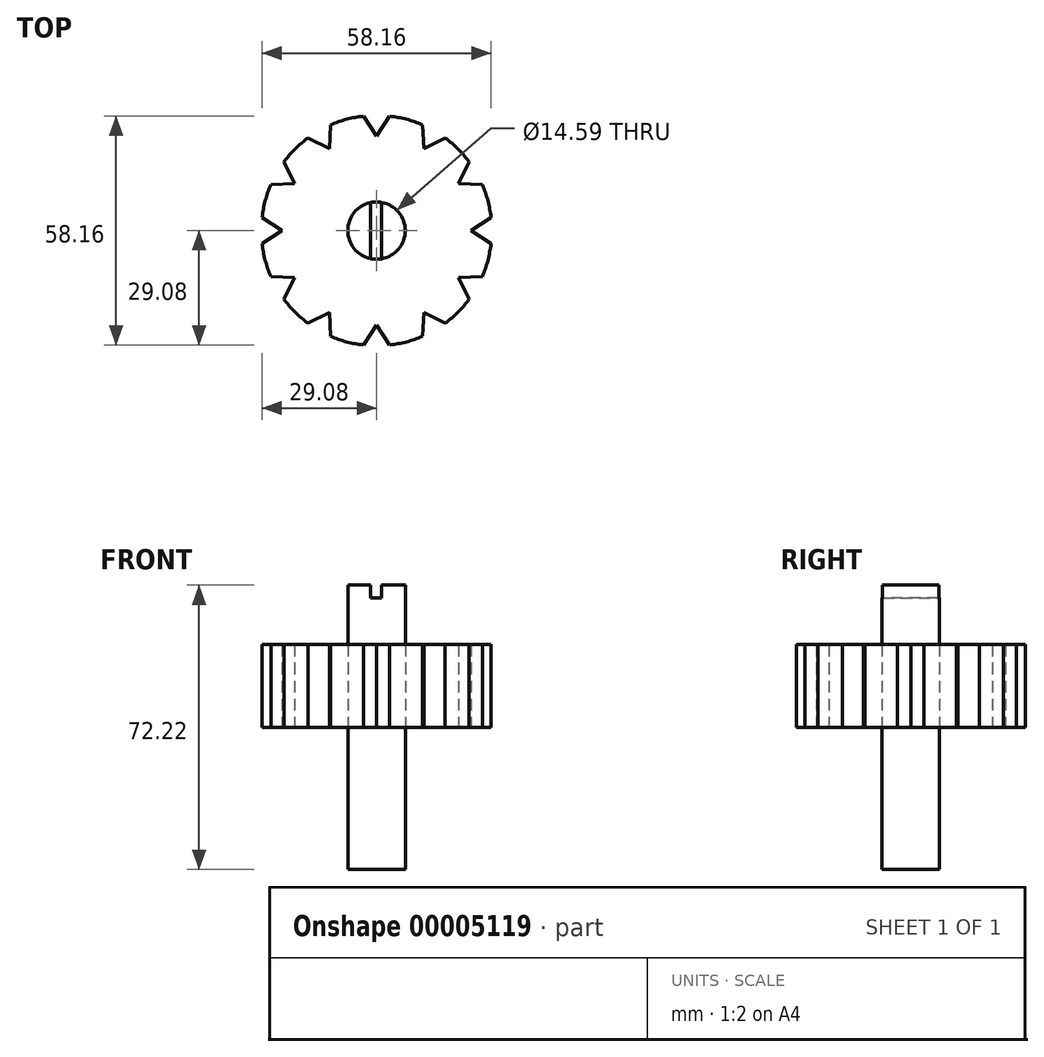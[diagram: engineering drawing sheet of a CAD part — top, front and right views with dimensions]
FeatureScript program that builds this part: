
annotation { "Feature Type Name" : "Feature", "Feature Type Description" : "" }
export const myFeature = defineFeature(function(context is Context, id is Id, definition is map)
    precondition{}
    {
        {
            var Q0;
            Q0=qCreatedBy(makeId("Top.planeOp"),FACE);
            var sketch = newSketch(context, id + "F0", { "sketchPlane" : qUnion([Q0])});
            skCircle(sketch, "E0", {"center": v(0, 0) * mm, "radius": 29.27 * mm});
            skCircle(sketch, "E1", {"center": v(0, 0) * mm, "radius": 7.3 * mm});
            skSolve(sketch);
        }
        {
            var Q0;
            Q0 = qSketchRegion(id + "F0", true);
            extrude(context, id + "F1", {"entities" : qUnion([Q0]), "depth" : 21.01 * mm});
        }
        {
            var Q0;
            Q0=qCreatedBy(makeId("Top.planeOp"),FACE);
            var sketch = newSketch(context, id + "F2", { "sketchPlane" : qUnion([Q0])});
            skCircle(sketch, "E2", {"center": v(0, 0) * mm, "radius": 7.3 * mm});
            skSolve(sketch);
        }
        {
            var Q0;
            Q0 = qSketchRegion(id + "F2", true);
            extrude(context, id + "F3", {"entities" : qUnion([Q0]), "endBound" : BoundingType.SYMMETRIC, "depth" : 72.2 * mm});
        }
        {
            var Q0;
            Q0=makeQuery(id+"F3.opExtrude","CAP_FACE",FACE,{"disambiguationData":[OSD([sQuery(id+"F2.wireOp",EDGE,"E2")])],"isStart":false});
            var sketch = newSketch(context, id + "F4", { "sketchPlane" : qUnion([Q0])});
            skLineSegment(sketch, "E3", {"start": v(-1.56, 10.01) * mm, "end": v(-1.56, -9.26) * mm});
            skLineSegment(sketch, "E4", {"start": v(-1.56, -9.26) * mm, "end": v(1.31, -9.26) * mm});
            skLineSegment(sketch, "E5", {"start": v(1.31, -9.26) * mm, "end": v(1.31, 9.87) * mm});
            skLineSegment(sketch, "E6", {"start": v(1.31, 9.87) * mm, "end": v(-1.56, 10.01) * mm});
            skSolve(sketch);
        }
        {
            var Q0;
            Q0 = qSketchRegion(id + "F4", true);
            extrude(context, id + "F5", {"entities" : qUnion([Q0]), "operationType" : NewBodyOperationType.REMOVE, "oppositeDirection" : true, "depth" : 3.3 * mm});
        }
        {
            var Q0;
            Q0=qCreatedBy(makeId("Top.planeOp"),FACE);
            var sketch = newSketch(context, id + "F6", { "sketchPlane" : qUnion([Q0])});
            skLineSegment(sketch, "E7", {"start": v(24, 0) * mm, "end": v(29.27, -3.46) * mm});
            skLineSegment(sketch, "E8", {"start": v(29.27, -3.46) * mm, "end": v(29.27, 3.46) * mm});
            skLineSegment(sketch, "E9", {"start": v(29.27, 3.46) * mm, "end": v(24, 0) * mm});
            skSolve(sketch);
        }
        {
            var Q0;
            Q0 = qSketchRegion(id + "F6", true);
            extrude(context, id + "F7", {"entities" : qUnion([Q0]), "endBound" : BoundingType.THROUGH_ALL, "depth" : 25.4 * mm});
        }
        {
            var Q0;
            Q0=makeQuery(id+"F7.opExtrude","SWEPT_BODY",BODY,{"disambiguationData":[OSD([sQuery(id+"F6.wireOp",EDGE,"E7"),sQuery(id+"F6.wireOp",EDGE,"E8"),sQuery(id+"F6.wireOp",EDGE,"E9")])]});
            var Q1;
            Q1=makeQuery(id+"F1.opExtrude","SWEPT_FACE",FACE,{"disambiguationData":[OSD([sQuery(id+"F0.wireOp",EDGE,"E0")])]});
            circularPattern(context, id + "F8", {"entities" : qUnion([Q0]), "axis" : qUnion([Q1]), "angle" : 30 * degree, "instanceCount" : 12});
        }
        {
            var Q0;
            Q0=makeQuery(id+"F8.opPattern","COPY",BODY,{"derivedFrom":makeQuery(id+"F7.opExtrude","SWEPT_BODY",BODY,{"disambiguationData":[OSD([sQuery(id+"F6.wireOp",EDGE,"E7"),sQuery(id+"F6.wireOp",EDGE,"E8"),sQuery(id+"F6.wireOp",EDGE,"E9")])]}),"instanceName":"9"});
            var Q1;
            Q1=makeQuery(id+"F8.opPattern","COPY",BODY,{"derivedFrom":makeQuery(id+"F7.opExtrude","SWEPT_BODY",BODY,{"disambiguationData":[OSD([sQuery(id+"F6.wireOp",EDGE,"E7"),sQuery(id+"F6.wireOp",EDGE,"E8"),sQuery(id+"F6.wireOp",EDGE,"E9")])]}),"instanceName":"10"});
            var Q2;
            Q2=makeQuery(id+"F8.opPattern","COPY",BODY,{"derivedFrom":makeQuery(id+"F7.opExtrude","SWEPT_BODY",BODY,{"disambiguationData":[OSD([sQuery(id+"F6.wireOp",EDGE,"E7"),sQuery(id+"F6.wireOp",EDGE,"E8"),sQuery(id+"F6.wireOp",EDGE,"E9")])]}),"instanceName":"11"});
            var Q3;
            Q3=makeQuery(id+"F7.opExtrude","SWEPT_BODY",BODY,{"disambiguationData":[OSD([sQuery(id+"F6.wireOp",EDGE,"E7"),sQuery(id+"F6.wireOp",EDGE,"E8"),sQuery(id+"F6.wireOp",EDGE,"E9")])]});
            var Q4;
            Q4=makeQuery(id+"F8.opPattern","COPY",BODY,{"derivedFrom":makeQuery(id+"F7.opExtrude","SWEPT_BODY",BODY,{"disambiguationData":[OSD([sQuery(id+"F6.wireOp",EDGE,"E7"),sQuery(id+"F6.wireOp",EDGE,"E8"),sQuery(id+"F6.wireOp",EDGE,"E9")])]}),"instanceName":"1"});
            var Q5;
            Q5=makeQuery(id+"F8.opPattern","COPY",BODY,{"derivedFrom":makeQuery(id+"F7.opExtrude","SWEPT_BODY",BODY,{"disambiguationData":[OSD([sQuery(id+"F6.wireOp",EDGE,"E7"),sQuery(id+"F6.wireOp",EDGE,"E8"),sQuery(id+"F6.wireOp",EDGE,"E9")])]}),"instanceName":"2"});
            var Q6;
            Q6=makeQuery(id+"F8.opPattern","COPY",BODY,{"derivedFrom":makeQuery(id+"F7.opExtrude","SWEPT_BODY",BODY,{"disambiguationData":[OSD([sQuery(id+"F6.wireOp",EDGE,"E7"),sQuery(id+"F6.wireOp",EDGE,"E8"),sQuery(id+"F6.wireOp",EDGE,"E9")])]}),"instanceName":"3"});
            var Q7;
            Q7=makeQuery(id+"F8.opPattern","COPY",BODY,{"derivedFrom":makeQuery(id+"F7.opExtrude","SWEPT_BODY",BODY,{"disambiguationData":[OSD([sQuery(id+"F6.wireOp",EDGE,"E7"),sQuery(id+"F6.wireOp",EDGE,"E8"),sQuery(id+"F6.wireOp",EDGE,"E9")])]}),"instanceName":"4"});
            var Q8;
            Q8=makeQuery(id+"F8.opPattern","COPY",BODY,{"derivedFrom":makeQuery(id+"F7.opExtrude","SWEPT_BODY",BODY,{"disambiguationData":[OSD([sQuery(id+"F6.wireOp",EDGE,"E7"),sQuery(id+"F6.wireOp",EDGE,"E8"),sQuery(id+"F6.wireOp",EDGE,"E9")])]}),"instanceName":"5"});
            var Q9;
            Q9=makeQuery(id+"F8.opPattern","COPY",BODY,{"derivedFrom":makeQuery(id+"F7.opExtrude","SWEPT_BODY",BODY,{"disambiguationData":[OSD([sQuery(id+"F6.wireOp",EDGE,"E7"),sQuery(id+"F6.wireOp",EDGE,"E8"),sQuery(id+"F6.wireOp",EDGE,"E9")])]}),"instanceName":"6"});
            var Q10;
            Q10=makeQuery(id+"F8.opPattern","COPY",BODY,{"derivedFrom":makeQuery(id+"F7.opExtrude","SWEPT_BODY",BODY,{"disambiguationData":[OSD([sQuery(id+"F6.wireOp",EDGE,"E7"),sQuery(id+"F6.wireOp",EDGE,"E8"),sQuery(id+"F6.wireOp",EDGE,"E9")])]}),"instanceName":"7"});
            var Q11;
            Q11=makeQuery(id+"F8.opPattern","COPY",BODY,{"derivedFrom":makeQuery(id+"F7.opExtrude","SWEPT_BODY",BODY,{"disambiguationData":[OSD([sQuery(id+"F6.wireOp",EDGE,"E7"),sQuery(id+"F6.wireOp",EDGE,"E8"),sQuery(id+"F6.wireOp",EDGE,"E9")])]}),"instanceName":"8"});
            var Q12;
            Q12=makeQuery(id+"F1.opExtrude","SWEPT_BODY",BODY,{"disambiguationData":[OSD([sQuery(id+"F0.wireOp",EDGE,"E0"),sQuery(id+"F0.wireOp",EDGE,"E1")])]});
            booleanBodies(context, id + "F9", {"operationType" : BooleanOperationType.SUBTRACTION, "tools" : qUnion([Q0, Q1, Q2, Q3, Q4, Q5, Q6, Q7, Q8, Q9, Q10, Q11]), "targets" : qUnion([Q12])});
        }
    });
